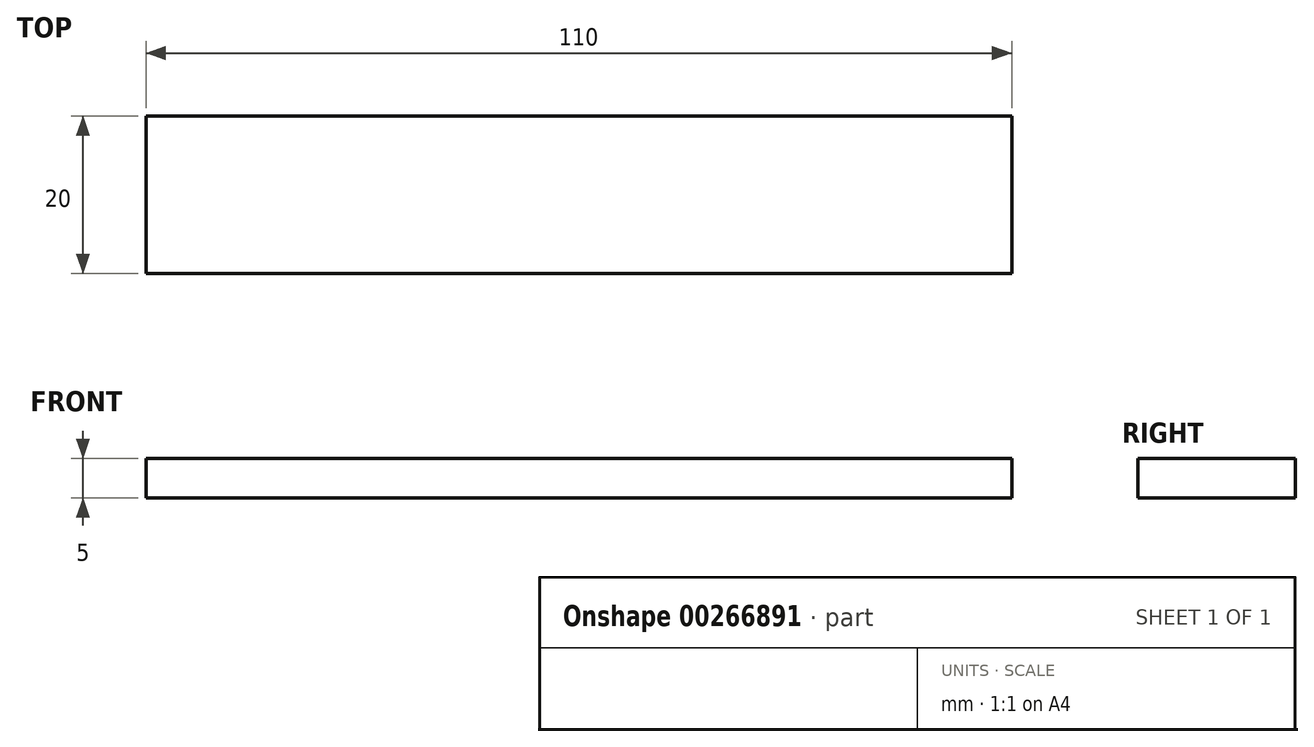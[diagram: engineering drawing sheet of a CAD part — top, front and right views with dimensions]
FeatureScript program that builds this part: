
annotation { "Feature Type Name" : "Feature", "Feature Type Description" : "" }
export const myFeature = defineFeature(function(context is Context, id is Id, definition is map)
    precondition{}
    {
        {
            var Q0;
            Q0=qCreatedBy(makeId("Right.planeOp"),FACE);
            var sketch = newSketch(context, id + "F0", { "sketchPlane" : qUnion([Q0])});
            skLineSegment(sketch, "E0.bottom", {"start": v(10, 2.5) * mm, "end": v(-10, 2.5) * mm});
            skLineSegment(sketch, "E0.top", {"start": v(10, -2.5) * mm, "end": v(-10, -2.5) * mm});
            skLineSegment(sketch, "E0.left", {"start": v(10, 2.5) * mm, "end": v(10, -2.5) * mm});
            skLineSegment(sketch, "E0.right", {"start": v(-10, 2.5) * mm, "end": v(-10, -2.5) * mm});
            skPoint(sketch, "E0.middle", {"position": v(0, 0) * mm});
            skSolve(sketch);
        }
        {
            var Q0;
            Q0 = qSketchRegion(id + "F0", true);
            extrude(context, id + "F1", {"entities" : qUnion([Q0]), "depth" : 110 * mm});
        }
    });
